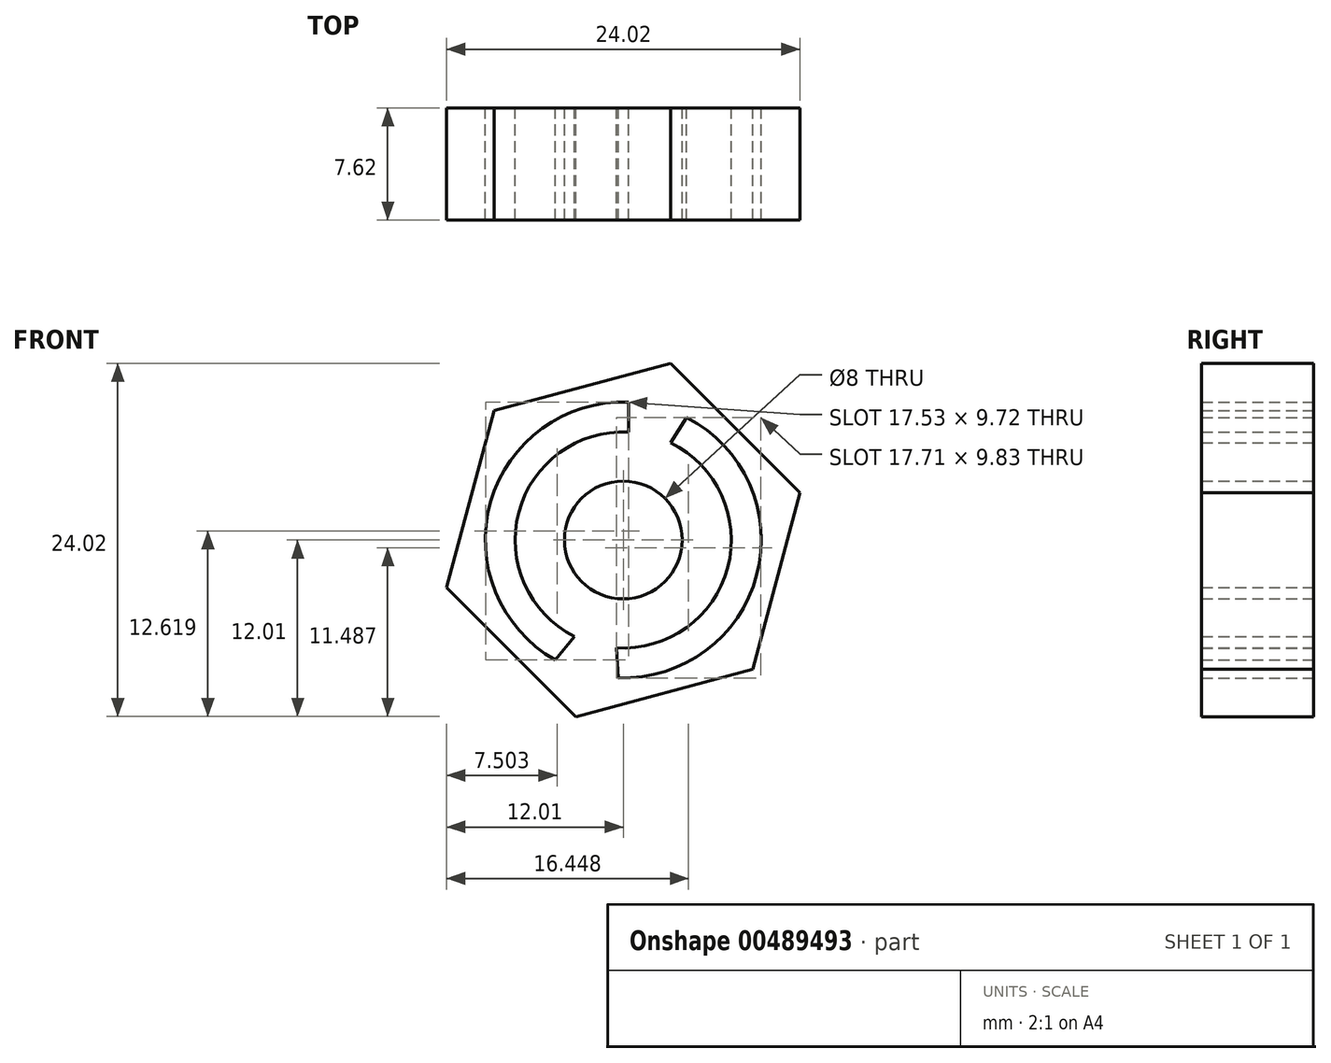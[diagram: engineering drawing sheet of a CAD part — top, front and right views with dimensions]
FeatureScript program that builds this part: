
annotation { "Feature Type Name" : "Feature", "Feature Type Description" : "" }
export const myFeature = defineFeature(function(context is Context, id is Id, definition is map)
    precondition{}
    {
        {
            var Q0;
            Q0=qCreatedBy(makeId("Front.planeOp"),FACE);
            var sketch = newSketch(context, id + "F0", { "sketchPlane" : qUnion([Q0])});
            skLineSegment(sketch, "E0.0", {"start": v(-9.48, 24.71) * mm, "end": v(-0.69, 15.92) * mm});
            skLineSegment(sketch, "E0.1", {"start": v(-0.69, 15.92) * mm, "end": v(-3.9, 3.9) * mm});
            skLineSegment(sketch, "E0.2", {"start": v(-3.9, 3.9) * mm, "end": v(-15.92, 0.69) * mm});
            skLineSegment(sketch, "E0.3", {"start": v(-15.92, 0.69) * mm, "end": v(-24.71, 9.48) * mm});
            skLineSegment(sketch, "E0.4", {"start": v(-24.71, 9.48) * mm, "end": v(-21.5, 21.5) * mm});
            skLineSegment(sketch, "E0.5", {"start": v(-21.5, 21.5) * mm, "end": v(-9.48, 24.71) * mm});
            skPoint(sketch, "E0.0.midPoint", {"position": v(-5.08, 20.32) * mm});
            skPoint(sketch, "E1.bottom.start.orphan", {"position": v(0, 0) * mm});
            skPoint(sketch, "E2.orphan", {"position": v(-25.4, 25.4) * mm});
            skPoint(sketch, "E0.cCircle.center.orphan", {"position": v(-12.7, 12.7) * mm});
            skSolve(sketch);
        }
        {
            var Q0;
            Q0=makeQuery(id+"F0.imprint","IMPRINT",FACE,{"disambiguationData":[TD([[makeQuery(id+"F0.imprint","IMPRINT",EDGE,{"derivedFrom":sQuery(id+"F0.wireOp",EDGE,"E0.0")}),-1.0]])]});
            extrude(context, id + "F1", {"entities" : qUnion([Q0]), "depth" : 7.62 * mm, "offsetDistance" : 25.4 * mm});
        }
        {
            var Q0;
            Q0=makeQuery(id+"F1.opExtrude","CAP_FACE",FACE,{"disambiguationData":[OSD([sQuery(id+"F0.wireOp",EDGE,"E0.0"),sQuery(id+"F0.wireOp",EDGE,"E0.1"),sQuery(id+"F0.wireOp",EDGE,"E0.2"),sQuery(id+"F0.wireOp",EDGE,"E0.3"),sQuery(id+"F0.wireOp",EDGE,"E0.4"),sQuery(id+"F0.wireOp",EDGE,"E0.5")])],"isStart":true});
            var sketch = newSketch(context, id + "F2", { "sketchPlane" : qUnion([Q0])});
            skLineSegment(sketch, "E3", {"start": v(9.48, 24.71) * mm, "end": v(15.92, 0.69) * mm});
            skCircle(sketch, "E4", {"center": v(12.7, 12.7) * mm, "radius": 4 * mm});
            skSolve(sketch);
        }
        {
            var Q0;
            {var subQ0=sQuery(id+"F2.wireOp",EDGE,"E4");var subQ1=sQuery(id+"F2.wireOp",EDGE,"E3");var subQ2=makeQuery(id+"F2.imprint","INTERSECT",VERTEX,{"disambiguationData":[OD(0.0)],"derivedFrom":[subQ1,subQ0]});Q0=makeQuery(id+"F2.imprint","IMPRINT",FACE,{"disambiguationData":[TD([[makeQuery(id+"F2.imprint","IMPRINT",EDGE,{"disambiguationData":[TD([[subQ2,-1.0]])],"derivedFrom":subQ1}),-1.0]])]});}
            var Q1;
            {var subQ0=sQuery(id+"F2.wireOp",EDGE,"E4");var subQ1=sQuery(id+"F2.wireOp",EDGE,"E3");var subQ2=makeQuery(id+"F2.imprint","INTERSECT",VERTEX,{"disambiguationData":[OD(0.0)],"derivedFrom":[subQ1,subQ0]});Q1=makeQuery(id+"F2.imprint","IMPRINT",FACE,{"disambiguationData":[TD([[makeQuery(id+"F2.imprint","IMPRINT",EDGE,{"disambiguationData":[TD([[subQ2,-1.0]])],"derivedFrom":subQ1}),1.0]])]});}
            extrude(context, id + "F3", {"entities" : qUnion([Q0, Q1]), "operationType" : NewBodyOperationType.REMOVE, "oppositeDirection" : true, "depth" : 7.62 * mm, "offsetDistance" : 25.4 * mm});
        }
        {
            var Q0;
            Q0=makeQuery(id+"F1.opExtrude","CAP_FACE",FACE,{"disambiguationData":[OSD([sQuery(id+"F0.wireOp",EDGE,"E0.0"),sQuery(id+"F0.wireOp",EDGE,"E0.1"),sQuery(id+"F0.wireOp",EDGE,"E0.2"),sQuery(id+"F0.wireOp",EDGE,"E0.3"),sQuery(id+"F0.wireOp",EDGE,"E0.4"),sQuery(id+"F0.wireOp",EDGE,"E0.5")])],"isStart":true});
            var sketch = newSketch(context, id + "F4", { "sketchPlane" : qUnion([Q0])});
            skCircle(sketch, "E5", {"center": v(12.7, 12.7) * mm, "radius": 9.38 * mm});
            skCircle(sketch, "E6", {"center": v(12.7, 12.7) * mm, "radius": 7.35 * mm});
            skLineSegment(sketch, "E7", {"start": v(12.35, 22.08) * mm, "end": v(12.35, 20.04) * mm});
            skLineSegment(sketch, "E8", {"start": v(8.38, 21.03) * mm, "end": v(9.48, 19.3) * mm});
            skLineSegment(sketch, "E9", {"start": v(13.18, 5.37) * mm, "end": v(13.03, 3.32) * mm});
            skLineSegment(sketch, "E10", {"start": v(16.03, 6.15) * mm, "end": v(17.33, 4.54) * mm});
            skSolve(sketch);
        }
        {
            var Q0;
            {var subQ0=sQuery(id+"F4.wireOp",EDGE,"E8");Q0=makeQuery(id+"F4.imprint","IMPRINT",FACE,{"disambiguationData":[TD([[makeQuery(id+"F4.imprint","IMPRINT",EDGE,{"derivedFrom":subQ0}),-1.0]])]});}
            var Q1;
            {var subQ0=sQuery(id+"F4.wireOp",EDGE,"E7");Q1=makeQuery(id+"F4.imprint","IMPRINT",FACE,{"disambiguationData":[TD([[makeQuery(id+"F4.imprint","IMPRINT",EDGE,{"derivedFrom":subQ0}),1.0]])]});}
            extrude(context, id + "F5", {"entities" : qUnion([Q0, Q1]), "operationType" : NewBodyOperationType.REMOVE, "oppositeDirection" : true, "depth" : 7.62 * mm, "offsetDistance" : 25.4 * mm});
        }
    });
